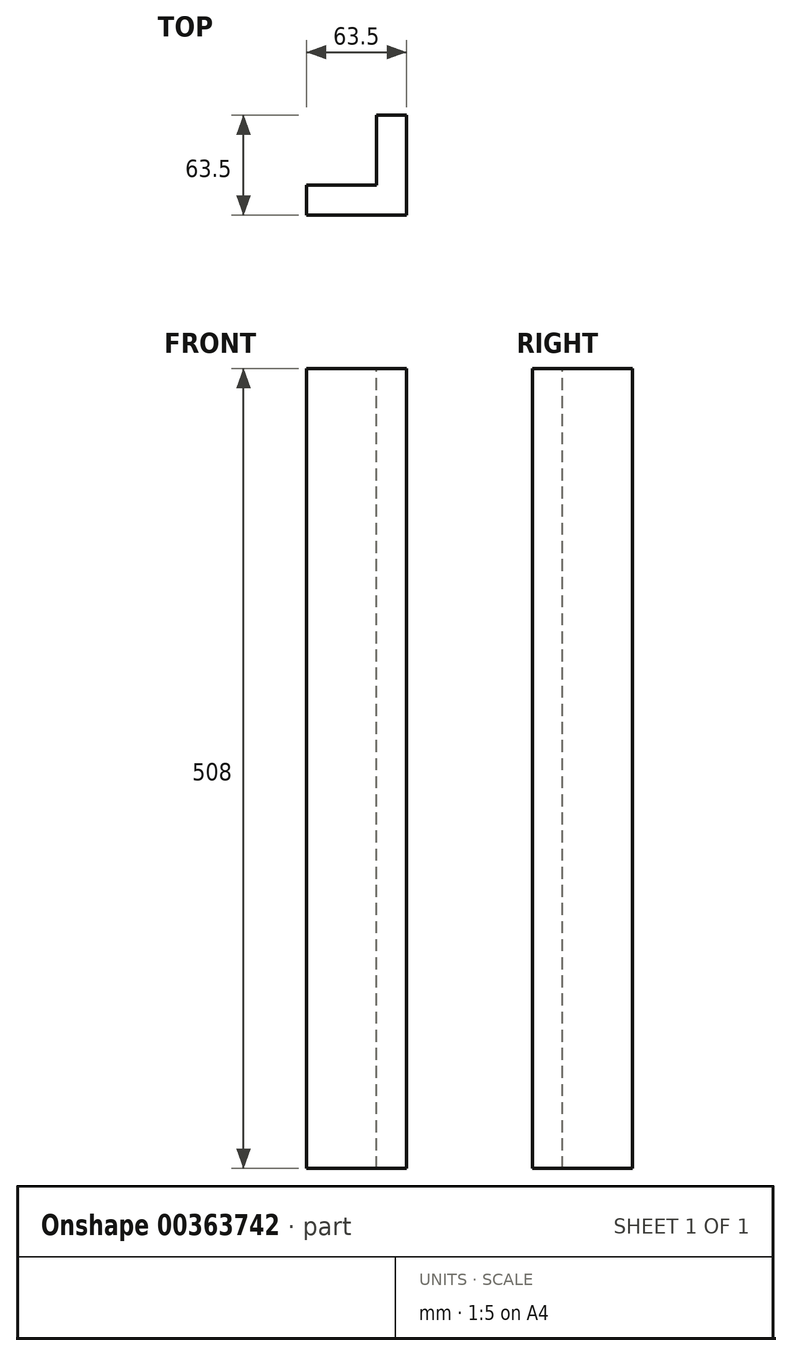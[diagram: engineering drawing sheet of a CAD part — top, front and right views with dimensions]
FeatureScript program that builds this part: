
annotation { "Feature Type Name" : "Feature", "Feature Type Description" : "" }
export const myFeature = defineFeature(function(context is Context, id is Id, definition is map)
    precondition{}
    {
        {
            var Q0;
            Q0=qCreatedBy(makeId("Front.planeOp"),FACE);
            var sketch = newSketch(context, id + "F0", { "sketchPlane" : qUnion([Q0])});
            skLineSegment(sketch, "E0.bottom", {"start": v(31.75, -254) * mm, "end": v(-31.75, -254) * mm});
            skLineSegment(sketch, "E0.top", {"start": v(31.75, 254) * mm, "end": v(-31.75, 254) * mm});
            skLineSegment(sketch, "E0.left", {"start": v(31.75, -254) * mm, "end": v(31.75, 254) * mm});
            skLineSegment(sketch, "E0.right", {"start": v(-31.75, -254) * mm, "end": v(-31.75, 254) * mm});
            skPoint(sketch, "E0.middle", {"position": v(0, 0) * mm});
            skSolve(sketch);
        }
        {
            var Q0;
            Q0 = qSketchRegion(id + "F0", true);
            extrude(context, id + "F1", {"entities" : qUnion([Q0]), "oppositeDirection" : true, "depth" : 19.05 * mm});
        }
        {
            var Q0;
            Q0=makeQuery(id+"F1.opExtrude","SWEPT_FACE",FACE,{"disambiguationData":[OSD([sQuery(id+"F0.wireOp",EDGE,"E0.left")])]});
            var sketch = newSketch(context, id + "F2", { "sketchPlane" : qUnion([Q0])});
            skLineSegment(sketch, "E1.bottom", {"start": v(19.05, 254) * mm, "end": v(63.5, 254) * mm});
            skLineSegment(sketch, "E1.top", {"start": v(19.05, -254) * mm, "end": v(63.5, -254) * mm});
            skLineSegment(sketch, "E1.left", {"start": v(19.05, 254) * mm, "end": v(19.05, -254) * mm});
            skLineSegment(sketch, "E1.right", {"start": v(63.5, 254) * mm, "end": v(63.5, -254) * mm});
            skSolve(sketch);
        }
        {
            var Q0;
            Q0 = qSketchRegion(id + "F2", true);
            extrude(context, id + "F3", {"entities" : qUnion([Q0]), "operationType" : NewBodyOperationType.ADD, "oppositeDirection" : true, "depth" : 19.05 * mm});
        }
    });
